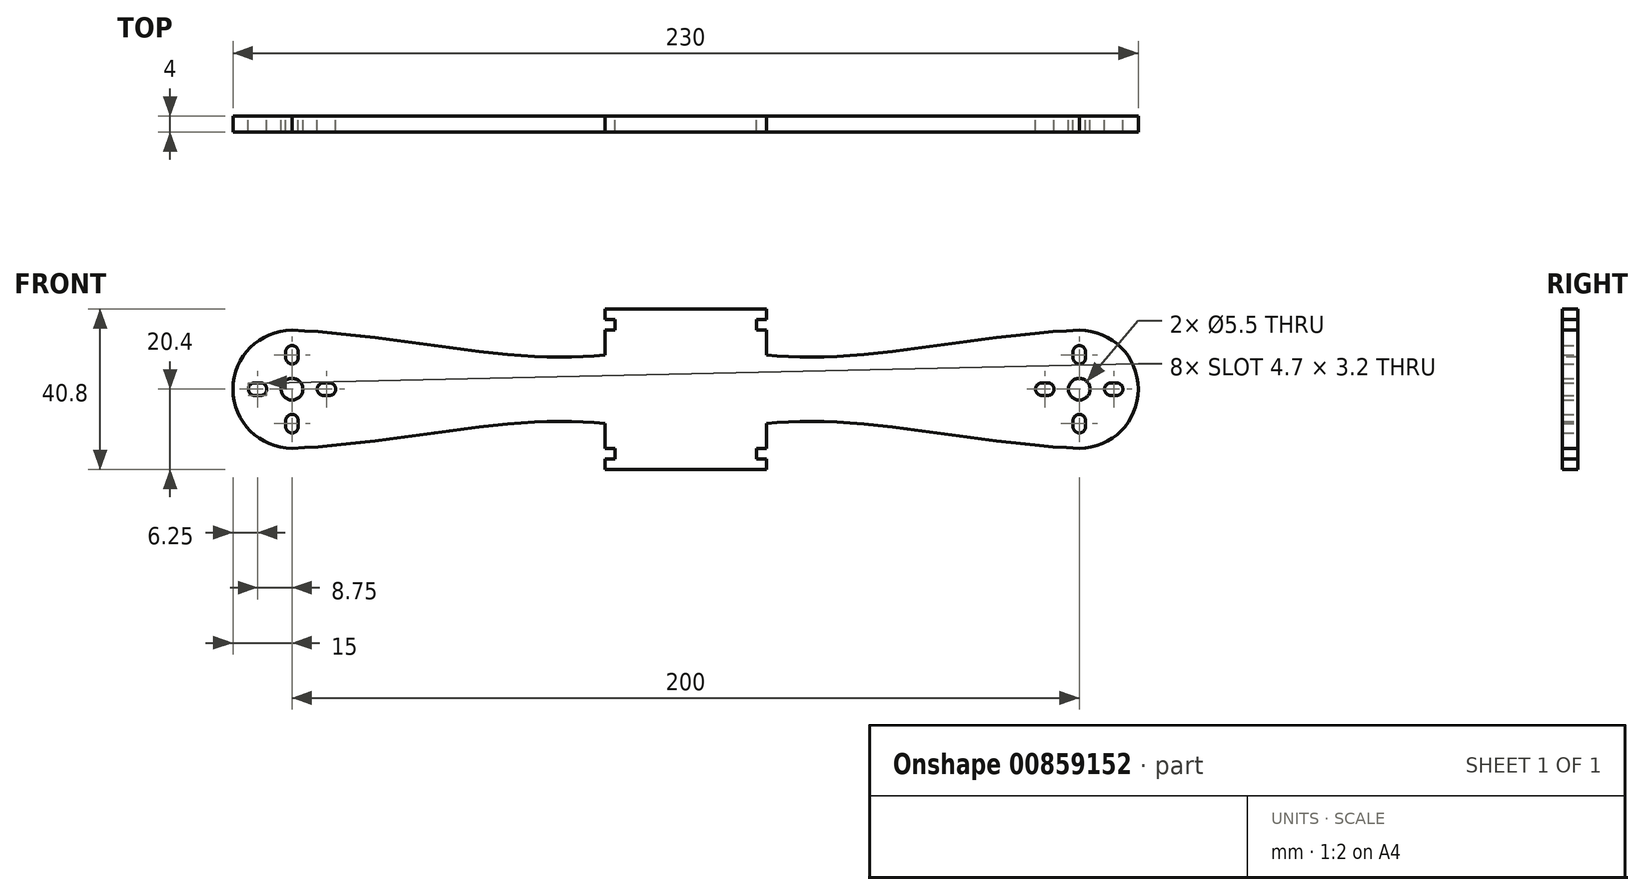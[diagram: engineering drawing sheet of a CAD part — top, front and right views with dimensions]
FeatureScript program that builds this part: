
annotation { "Feature Type Name" : "Feature", "Feature Type Description" : "" }
export const myFeature = defineFeature(function(context is Context, id is Id, definition is map)
    precondition{}
    {
        {
            var Q0;
            Q0=qCreatedBy(makeId("Front.planeOp"),FACE);
            var sketch = newSketch(context, id + "F0", { "sketchPlane" : qUnion([Q0])});
            skLineSegment(sketch, "E0", {"start": v(0, 200.75) * mm, "end": v(0, -183.56) * mm, "construction": true});
            skLineSegment(sketch, "E1", {"start": v(-221.9, 0) * mm, "end": v(251, 0) * mm, "construction": true});
            skCircle(sketch, "E2", {"center": v(-100, 80) * mm, "radius": 64.5 * mm, "construction": true});
            skCircle(sketch, "E3.MirrorC", {"center": v(100, 80) * mm, "radius": 64.5 * mm, "construction": true});
            skLineSegment(sketch, "E4.bottom", {"start": v(-18, 100) * mm, "end": v(18, 100) * mm, "construction": true});
            skLineSegment(sketch, "E4.left", {"start": v(-18, 100) * mm, "end": v(-18, 95) * mm, "construction": true});
            skLineSegment(sketch, "E4.right", {"start": v(18, 100) * mm, "end": v(18, -100) * mm, "construction": true});
            skLineSegment(sketch, "E5", {"start": v(0, 80) * mm, "end": v(-100, 80) * mm, "construction": true});
            skCircle(sketch, "E6.MirrorC", {"center": v(100, -80) * mm, "radius": 64.5 * mm, "construction": true});
            skCircle(sketch, "E7.MirrorC", {"center": v(-100, -80) * mm, "radius": 64.5 * mm, "construction": true});
            skLineSegment(sketch, "E8", {"start": v(-100, 80) * mm, "end": v(-100, 0) * mm, "construction": true});
            skArc(sketch, "E9", {"start": v(-100, 95) * mm, "mid": v(-115, 80) * mm, "end": v(-100, 65) * mm});
            skArc(sketch, "E10.MirrorC", {"start": v(100, 95) * mm, "mid": v(115, 80) * mm, "end": v(100, 65) * mm});
            skFitSpline(sketch, "E11", {"points": [v(-100, 95) * mm, v(-36.43, 88.25) * mm, v(0, 92.54) * mm], "startDerivative": vector(98.63, -3.04) * mm, "endDerivative": vector(79.5, 18.83) * mm});
            skFitSpline(sketch, "E12.MirrorCS", {"points": [v(-100, 65) * mm, v(-36.43, 71.75) * mm, v(0, 67.46) * mm], "startDerivative": vector(98.63, 3.04) * mm, "endDerivative": vector(79.5, -18.83) * mm});
            skFitSpline(sketch, "E13.MirrorCS", {"points": [v(100, 95) * mm, v(36.43, 88.25) * mm, v(0, 92.54) * mm], "startDerivative": vector(-98.63, -3.04) * mm, "endDerivative": vector(-79.5, 18.83) * mm});
            skFitSpline(sketch, "E14.MirrorCS", {"points": [v(100, 65) * mm, v(36.43, 71.75) * mm, v(0, 67.46) * mm], "startDerivative": vector(-98.63, 3.04) * mm, "endDerivative": vector(-79.5, -18.83) * mm});
            skCircle(sketch, "E15", {"center": v(-100, 80) * mm, "radius": 2.75 * mm});
            skLineSegment(sketch, "E16", {"start": v(-100, 103.48) * mm, "end": v(-100, 52.83) * mm, "construction": true});
            skLineSegment(sketch, "E17", {"start": v(-107.97, 80) * mm, "end": v(-71.59, 80) * mm, "construction": true});
            skCircle(sketch, "E18", {"center": v(-100, 80) * mm, "radius": 8 * mm, "construction": true});
            skCircle(sketch, "E19", {"center": v(-100, 80) * mm, "radius": 9.5 * mm, "construction": true});
            skArc(sketch, "E20", {"start": v(-98.4, 89.5) * mm, "mid": v(-100, 91.1) * mm, "end": v(-101.6, 89.5) * mm});
            skArc(sketch, "E21", {"start": v(-101.6, 88) * mm, "mid": v(-100, 86.4) * mm, "end": v(-98.4, 88) * mm});
            skLineSegment(sketch, "E22", {"start": v(-101.6, 89.5) * mm, "end": v(-101.6, 88) * mm});
            skLineSegment(sketch, "E23.MirrorCS", {"start": v(-98.4, 89.5) * mm, "end": v(-98.4, 88) * mm});
            skArc(sketch, "E24.MirrorCS", {"start": v(-98.4, 70.5) * mm, "mid": v(-100, 68.9) * mm, "end": v(-101.6, 70.5) * mm});
            skLineSegment(sketch, "E25.MirrorCS", {"start": v(-101.6, 70.5) * mm, "end": v(-101.6, 72) * mm});
            skArc(sketch, "E26.MirrorCS", {"start": v(-101.6, 72) * mm, "mid": v(-100, 73.6) * mm, "end": v(-98.4, 72) * mm});
            skLineSegment(sketch, "E27.MirrorCS", {"start": v(-98.4, 70.5) * mm, "end": v(-98.4, 72) * mm});
            skLineSegment(sketch, "E28", {"start": v(-109.23, 70.77) * mm, "end": v(-91.44, 88.56) * mm, "construction": true});
            skArc(sketch, "E29.MirrorCS", {"start": v(-92, 78.4) * mm, "mid": v(-93.6, 80) * mm, "end": v(-92, 81.6) * mm});
            skArc(sketch, "E30.MirrorCS", {"start": v(-90.5, 81.6) * mm, "mid": v(-88.9, 80) * mm, "end": v(-90.5, 78.4) * mm});
            skLineSegment(sketch, "E31.MirrorCS", {"start": v(-90.5, 78.4) * mm, "end": v(-92, 78.4) * mm});
            skLineSegment(sketch, "E32.MirrorCS", {"start": v(-90.5, 81.6) * mm, "end": v(-92, 81.6) * mm});
            skArc(sketch, "E33.MirrorCS", {"start": v(-109.5, 81.6) * mm, "mid": v(-111.1, 80) * mm, "end": v(-109.5, 78.4) * mm});
            skLineSegment(sketch, "E34.MirrorCS", {"start": v(-109.5, 78.4) * mm, "end": v(-108, 78.4) * mm});
            skArc(sketch, "E35.MirrorCS", {"start": v(-108, 78.4) * mm, "mid": v(-106.4, 80) * mm, "end": v(-108, 81.6) * mm});
            skLineSegment(sketch, "E36.MirrorCS", {"start": v(-109.5, 81.6) * mm, "end": v(-108, 81.6) * mm});
            skLineSegment(sketch, "E37.MirrorCS", {"start": v(98.4, 89.5) * mm, "end": v(98.4, 88) * mm});
            skLineSegment(sketch, "E38.MirrorCS", {"start": v(101.6, 89.5) * mm, "end": v(101.6, 88) * mm});
            skLineSegment(sketch, "E39.MirrorCS", {"start": v(90.5, 81.6) * mm, "end": v(92, 81.6) * mm});
            skLineSegment(sketch, "E40.MirrorCS", {"start": v(90.5, 78.4) * mm, "end": v(92, 78.4) * mm});
            skLineSegment(sketch, "E41.MirrorCS", {"start": v(101.6, 70.5) * mm, "end": v(101.6, 72) * mm});
            skLineSegment(sketch, "E42.MirrorCS", {"start": v(98.4, 70.5) * mm, "end": v(98.4, 72) * mm});
            skArc(sketch, "E43.MirrorCS", {"start": v(101.6, 72) * mm, "mid": v(100, 73.6) * mm, "end": v(98.4, 72) * mm});
            skArc(sketch, "E44.MirrorCS", {"start": v(90.5, 81.6) * mm, "mid": v(88.9, 80) * mm, "end": v(90.5, 78.4) * mm});
            skArc(sketch, "E45.MirrorCS", {"start": v(108, 78.4) * mm, "mid": v(106.4, 80) * mm, "end": v(108, 81.6) * mm});
            skArc(sketch, "E46.MirrorCS", {"start": v(92, 78.4) * mm, "mid": v(93.6, 80) * mm, "end": v(92, 81.6) * mm});
            skArc(sketch, "E47.MirrorCS", {"start": v(101.6, 88) * mm, "mid": v(100, 86.4) * mm, "end": v(98.4, 88) * mm});
            skCircle(sketch, "E48.MirrorC", {"center": v(100, 80) * mm, "radius": 2.75 * mm});
            skCircle(sketch, "E49.MirrorC", {"center": v(100, 80) * mm, "radius": 8 * mm, "construction": true});
            skArc(sketch, "E50.MirrorCS", {"start": v(98.4, 70.5) * mm, "mid": v(100, 68.9) * mm, "end": v(101.6, 70.5) * mm});
            skLineSegment(sketch, "E51.MirrorCS", {"start": v(109.23, 70.77) * mm, "end": v(91.44, 88.56) * mm, "construction": true});
            skArc(sketch, "E52.MirrorCS", {"start": v(98.4, 89.5) * mm, "mid": v(100, 91.1) * mm, "end": v(101.6, 89.5) * mm});
            skArc(sketch, "E53.MirrorCS", {"start": v(109.5, 81.6) * mm, "mid": v(111.1, 80) * mm, "end": v(109.5, 78.4) * mm});
            skLineSegment(sketch, "E54.MirrorCS", {"start": v(109.5, 81.6) * mm, "end": v(108, 81.6) * mm});
            skLineSegment(sketch, "E55.MirrorCS", {"start": v(109.5, 78.4) * mm, "end": v(108, 78.4) * mm});
            skCircle(sketch, "E56.MirrorC", {"center": v(100, 80) * mm, "radius": 9.5 * mm, "construction": true});
            skPoint(sketch, "E57.orphan", {"position": v(-1.26, 92.24) * mm});
            skPoint(sketch, "E58.visualSharp", {"position": v(-15.16, 90.52) * mm});
            skPoint(sketch, "E59.visualSharp", {"position": v(-15.19, 89.45) * mm});
            skPoint(sketch, "E60.MirrorP", {"position": v(1.26, 92.24) * mm});
            skPoint(sketch, "E61.MirrorP", {"position": v(1.26, 67.76) * mm});
            skPoint(sketch, "E62.MirrorP", {"position": v(-1.26, 67.76) * mm});
            skLineSegment(sketch, "E63.MirrorCS", {"start": v(-221.9, 185.04) * mm, "end": v(251, 185.04) * mm, "construction": true});
            skPoint(sketch, "E58.filletArc.end.orphan", {"position": v(-15.66, 90.52) * mm});
            skPoint(sketch, "E64.start.orphan", {"position": v(-15.16, 90.02) * mm});
            skPoint(sketch, "E59.filletArc.end.orphan", {"position": v(-15.16, 89.65) * mm});
            skPoint(sketch, "E59.filletArc.start.orphan", {"position": v(-18, 89.05) * mm});
            skPoint(sketch, "E65.orphan", {"position": v(-15.19, 70.55) * mm});
            skPoint(sketch, "E66.orphan", {"position": v(15.19, 70.55) * mm});
            skLineSegment(sketch, "E67", {"start": v(-18, 95) * mm, "end": v(-18, 89.05) * mm});
            skLineSegment(sketch, "E68.MirrorCS", {"start": v(18, 95) * mm, "end": v(18, 89.05) * mm});
            skLineSegment(sketch, "E69.MirrorCS", {"start": v(-18, 65) * mm, "end": v(-18, 70.95) * mm});
            skLineSegment(sketch, "E70.MirrorCS", {"start": v(18, 65) * mm, "end": v(18, 70.95) * mm});
            skLineSegment(sketch, "E71.bottom", {"start": v(-17, 15.5) * mm, "end": v(17, 15.5) * mm, "construction": true});
            skLineSegment(sketch, "E71.left", {"start": v(-17, 15.5) * mm, "end": v(-17, -54.5) * mm, "construction": true});
            skLineSegment(sketch, "E71.right", {"start": v(17, 15.5) * mm, "end": v(17, -54.5) * mm, "construction": true});
            skLineSegment(sketch, "E72.bottom", {"start": v(-20.5, 100.4) * mm, "end": v(20.5, 100.4) * mm});
            skLineSegment(sketch, "E72.top", {"start": v(-20.5, 97.7) * mm, "end": v(-18, 97.7) * mm});
            skLineSegment(sketch, "E72.left", {"start": v(-20.5, 100.4) * mm, "end": v(-20.5, 97.7) * mm});
            skLineSegment(sketch, "E72.right", {"start": v(20.5, 100.4) * mm, "end": v(20.5, 97.7) * mm});
            skLineSegment(sketch, "E73", {"start": v(-18, 95) * mm, "end": v(-20.5, 95) * mm});
            skLineSegment(sketch, "E74", {"start": v(-20.5, 95) * mm, "end": v(-20.5, 88.76) * mm});
            skLineSegment(sketch, "E75.MirrorCS", {"start": v(20.5, 95) * mm, "end": v(20.5, 88.76) * mm});
            skLineSegment(sketch, "E76.MirrorCS", {"start": v(18, 95) * mm, "end": v(20.5, 95) * mm});
            skLineSegment(sketch, "E77", {"start": v(-18, 97.7) * mm, "end": v(-18, 95) * mm});
            skLineSegment(sketch, "E78.MirrorCS", {"start": v(18, 97.7) * mm, "end": v(18, 95) * mm});
            skLineSegment(sketch, "E79.trimOffspring", {"start": v(18, 97.7) * mm, "end": v(20.5, 97.7) * mm});
            skPoint(sketch, "E80.orphan", {"position": v(18, 95) * mm});
            skLineSegment(sketch, "E81.trimOffspring", {"start": v(-18, 89.05) * mm, "end": v(-18, -100) * mm, "construction": true});
            skPoint(sketch, "E82.orphan", {"position": v(18, 89.05) * mm});
            skPoint(sketch, "E83.MirrorP", {"position": v(-15.16, 69.98) * mm});
            skLineSegment(sketch, "E84.MirrorCS", {"start": v(-18, 62.3) * mm, "end": v(-18, 65) * mm});
            skPoint(sketch, "E85.MirrorP", {"position": v(-18, 70.95) * mm});
            skPoint(sketch, "E86.MirrorP", {"position": v(18, 65) * mm});
            skLineSegment(sketch, "E87.MirrorCS", {"start": v(-20.5, 65) * mm, "end": v(-20.5, 71.24) * mm});
            skLineSegment(sketch, "E88.MirrorCS", {"start": v(-20.5, 59.6) * mm, "end": v(20.5, 59.6) * mm});
            skPoint(sketch, "E89.MirrorP", {"position": v(-15.66, 69.48) * mm});
            skLineSegment(sketch, "E90.MirrorCS", {"start": v(-20.5, 62.3) * mm, "end": v(-18, 62.3) * mm});
            skPoint(sketch, "E91.MirrorP", {"position": v(-15.16, 70.35) * mm});
            skLineSegment(sketch, "E92.MirrorCS", {"start": v(18, 62.3) * mm, "end": v(20.5, 62.3) * mm});
            skLineSegment(sketch, "E93.MirrorCS", {"start": v(20.5, 65) * mm, "end": v(20.5, 71.24) * mm});
            skPoint(sketch, "E94.MirrorP", {"position": v(-15.16, 69.48) * mm});
            skLineSegment(sketch, "E95.MirrorCS", {"start": v(-18, 60) * mm, "end": v(-18, 65) * mm, "construction": true});
            skLineSegment(sketch, "E96.MirrorCS", {"start": v(-18, 60) * mm, "end": v(18, 60) * mm, "construction": true});
            skLineSegment(sketch, "E97.MirrorCS", {"start": v(18, 65) * mm, "end": v(20.5, 65) * mm});
            skLineSegment(sketch, "E98.MirrorCS", {"start": v(-20.5, 59.6) * mm, "end": v(-20.5, 62.3) * mm});
            skPoint(sketch, "E99.MirrorP", {"position": v(18, 70.95) * mm});
            skLineSegment(sketch, "E100.MirrorCS", {"start": v(18, 62.3) * mm, "end": v(18, 65) * mm});
            skLineSegment(sketch, "E101.MirrorCS", {"start": v(20.5, 59.6) * mm, "end": v(20.5, 62.3) * mm});
            skLineSegment(sketch, "E102.MirrorCS", {"start": v(-18, 65) * mm, "end": v(-20.5, 65) * mm});
            skPoint(sketch, "E103.trimOffspring.end.orphan", {"position": v(16.03, 70.68) * mm});
            skPoint(sketch, "E104.orphan", {"position": v(-18, 65) * mm});
            skSolve(sketch);
        }
        {
            var Q0;
            Q0 = qSketchRegion(id + "F0", true);
            extrude(context, id + "F1", {"entities" : qUnion([Q0]), "depth" : 4 * mm, "offsetDistance" : 25 * mm});
        }
    });
